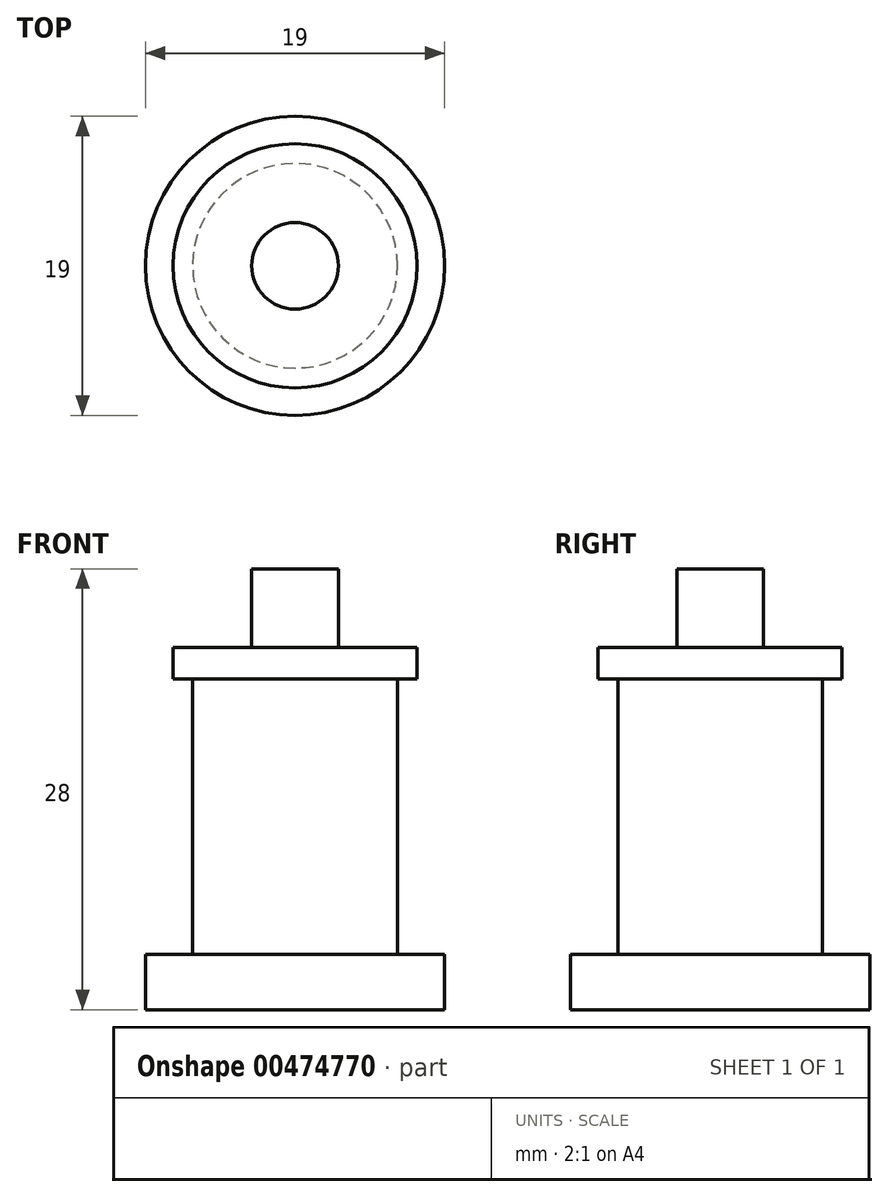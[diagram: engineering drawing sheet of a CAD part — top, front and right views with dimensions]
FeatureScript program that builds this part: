
annotation { "Feature Type Name" : "Feature", "Feature Type Description" : "" }
export const myFeature = defineFeature(function(context is Context, id is Id, definition is map)
    precondition{}
    {
        {
            var Q0;
            Q0=qCreatedBy(makeId("Front.planeOp"),FACE);
            var sketch = newSketch(context, id + "F0", { "sketchPlane" : qUnion([Q0])});
            skLineSegment(sketch, "E0", {"start": v(0, 0) * mm, "end": v(0, 28) * mm});
            skLineSegment(sketch, "E1", {"start": v(0, 0) * mm, "end": v(9.5, 0) * mm});
            skLineSegment(sketch, "E2", {"start": v(9.5, 0) * mm, "end": v(9.5, 3.5) * mm});
            skLineSegment(sketch, "E3", {"start": v(9.5, 3.5) * mm, "end": v(6.5, 3.5) * mm});
            skLineSegment(sketch, "E4", {"start": v(6.5, 3.5) * mm, "end": v(6.5, 21) * mm});
            skLineSegment(sketch, "E5", {"start": v(6.5, 21) * mm, "end": v(7.75, 21) * mm});
            skLineSegment(sketch, "E6", {"start": v(7.75, 21) * mm, "end": v(7.75, 23) * mm});
            skLineSegment(sketch, "E7", {"start": v(7.75, 23) * mm, "end": v(2.75, 23) * mm});
            skLineSegment(sketch, "E8", {"start": v(2.75, 23) * mm, "end": v(2.75, 28) * mm});
            skLineSegment(sketch, "E9", {"start": v(2.75, 28) * mm, "end": v(0, 28) * mm});
            skLineSegment(sketch, "E10", {"start": v(0, 28) * mm, "end": v(0, 33) * mm, "construction": true});
            skSolve(sketch);
        }
        {
            var Q0;
            Q0 = qSketchRegion(id + "F0", true);
            var Q1;
            Q1=sQuery(id+"F0.wireOp",EDGE,"E10");
            revolve(context, id + "F1", {"entities" : qUnion([Q0]), "axis" : qUnion([Q1]), "revolveType" : RevolveType.FULL});
        }
    });
